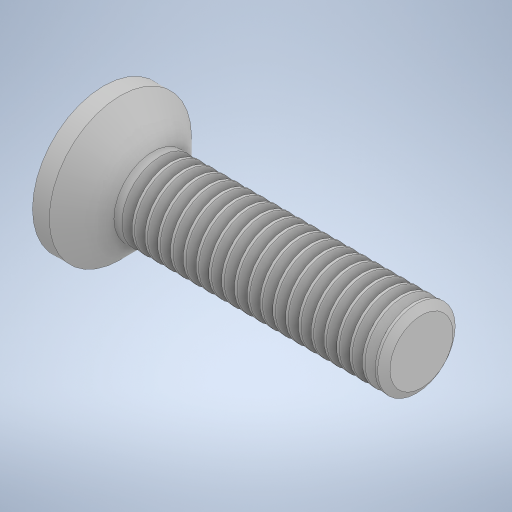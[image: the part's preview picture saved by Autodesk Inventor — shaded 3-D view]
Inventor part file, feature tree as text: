
AUTODESK INVENTOR PART (.ipt)
format: ipt  version: 2023 (Build 270158000, 158)  size: 373,248 bytes
history: mixed  units: in
note: dims shown in document units (in); Inventor stores cm internally (conversion verified against a paired STEP export)
features: extrude x1, sketch x1, imported_body x1
ambient origin geometry x8: Origin, YZ Plane, XZ Plane, XY Plane, X Axis, Y Axis, Z Axis, Center Point
bodies: Solid1 (imported_parasolid), Body1 (imported_parasolid)
feature tree (3):
  extrude  "Extrusion2"  TaperAngle=0.0deg  [1 undecoded]
  sketch  "Sketch2"  dims[d6=0.409in d7=0.0in d8=0.1969in d9=0.1969in d10=0.0in d11=0.0in]
  imported_body  NMx_Import_Brep_tag  [imported B-rep: ~79 faces, bbox_mm=[12.793478, 3.198662, 4.349331]]
note: 1 required parameter value undecoded (feature->parameter linkage not recoverable at this tier; creation-order binding heuristic only, values carry confidence <= 0.55)
